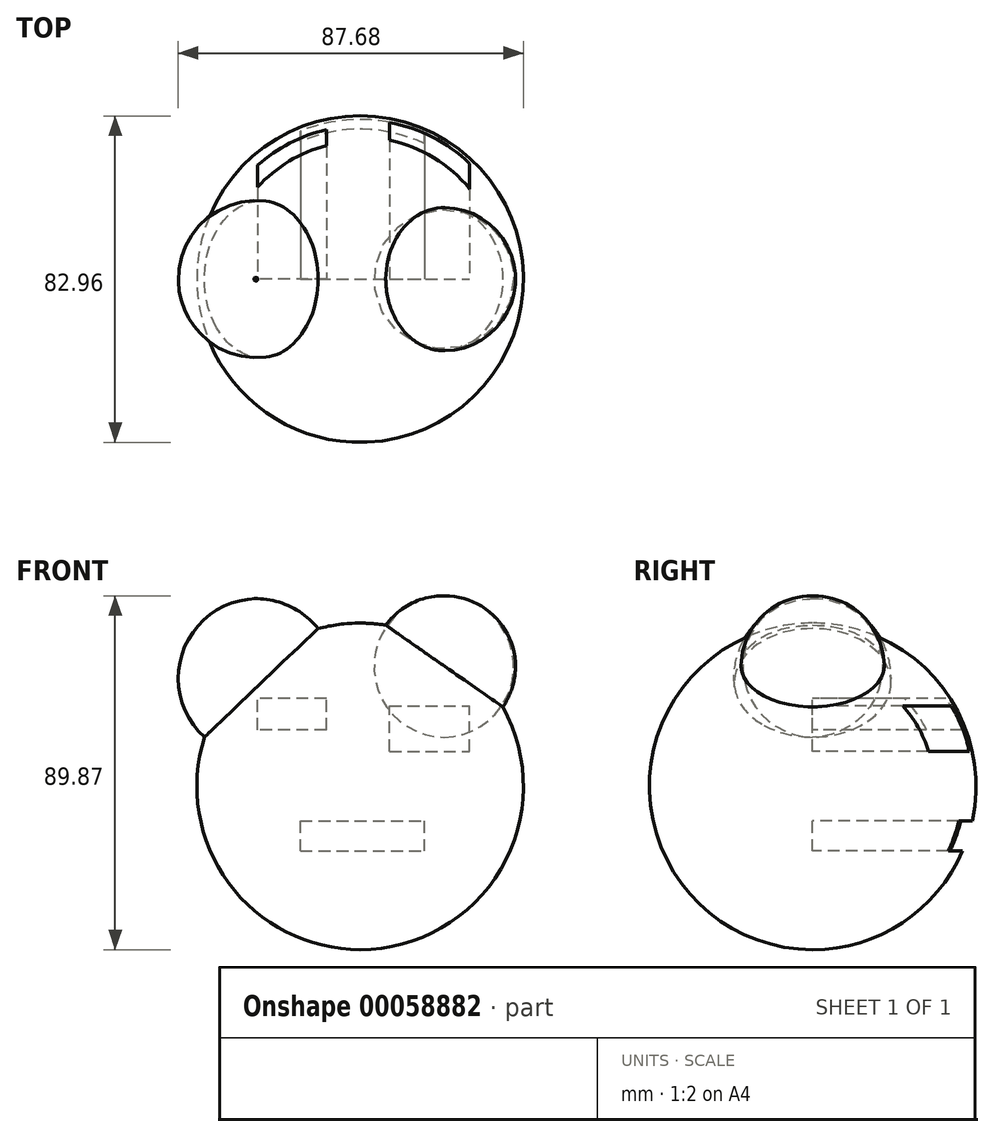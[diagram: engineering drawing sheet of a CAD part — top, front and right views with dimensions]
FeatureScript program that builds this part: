
annotation { "Feature Type Name" : "Feature", "Feature Type Description" : "" }
export const myFeature = defineFeature(function(context is Context, id is Id, definition is map)
    precondition{}
    {
        {
            var Q0;
            Q0=qCreatedBy(makeId("Front.planeOp"),FACE);
            var sketch = newSketch(context, id + "F0", { "sketchPlane" : qUnion([Q0])});
            skCircle(sketch, "E0", {"center": v(0, 0) * mm, "radius": 41.48 * mm});
            skLineSegment(sketch, "E1", {"start": v(0, -41.48) * mm, "end": v(0, 41.48) * mm});
            skSolve(sketch);
        }
        {
            var Q0;
            {var subQ0=sQuery(id+"F0.wireOp",EDGE,"E1");Q0=makeQuery(id+"F0.imprint","IMPRINT",FACE,{"disambiguationData":[TD([[makeQuery(id+"F0.imprint","IMPRINT",EDGE,{"derivedFrom":subQ0}),1.0]])]});}
            var Q1;
            Q1=sQuery(id+"F0.wireOp",EDGE,"E1");
            revolve(context, id + "F1", {"entities" : qUnion([Q0]), "axis" : qUnion([Q1]), "revolveType" : RevolveType.FULL});
        }
        {
            var Q0;
            Q0=qCreatedBy(makeId("Front.planeOp"),FACE);
            var sketch = newSketch(context, id + "F2", { "sketchPlane" : qUnion([Q0])});
            skCircle(sketch, "E2", {"center": v(-26.48, 27.5) * mm, "radius": 20.19 * mm});
            skLineSegment(sketch, "E3", {"start": v(-26, 7.32) * mm, "end": v(-26.48, 47.69) * mm});
            skSolve(sketch);
        }
        {
            var Q0;
            {var subQ0=sQuery(id+"F2.wireOp",EDGE,"E3");Q0=makeQuery(id+"F2.imprint","IMPRINT",FACE,{"disambiguationData":[TD([[makeQuery(id+"F2.imprint","IMPRINT",EDGE,{"derivedFrom":subQ0}),-1.0]])]});}
            var Q1;
            Q1=sQuery(id+"F2.wireOp",EDGE,"E3");
            revolve(context, id + "F3", {"operationType" : NewBodyOperationType.ADD, "entities" : qUnion([Q0]), "axis" : qUnion([Q1]), "revolveType" : RevolveType.FULL});
        }
        {
            var Q0;
            Q0=qCreatedBy(makeId("Front.planeOp"),FACE);
            var sketch = newSketch(context, id + "F4", { "sketchPlane" : qUnion([Q0])});
            skCircle(sketch, "E4", {"center": v(21.5, 30.44) * mm, "radius": 17.95 * mm});
            skLineSegment(sketch, "E5", {"start": v(21.27, 12.5) * mm, "end": v(21.27, 48.4) * mm});
            skSolve(sketch);
        }
        {
            var Q0;
            {var subQ0=sQuery(id+"F4.wireOp",EDGE,"E5");Q0=makeQuery(id+"F4.imprint","IMPRINT",FACE,{"disambiguationData":[TD([[makeQuery(id+"F4.imprint","IMPRINT",EDGE,{"derivedFrom":subQ0}),-1.0]])]});}
            var Q1;
            Q1=sQuery(id+"F4.wireOp",EDGE,"E5");
            revolve(context, id + "F5", {"operationType" : NewBodyOperationType.ADD, "entities" : qUnion([Q0]), "axis" : qUnion([Q1]), "revolveType" : RevolveType.FULL});
        }
        {
            var Q0;
            Q0=qCreatedBy(makeId("Front.planeOp"),FACE);
            var sketch = newSketch(context, id + "F6", { "sketchPlane" : qUnion([Q0])});
            skLineSegment(sketch, "E6.bottom", {"start": v(-8.6, 14.37) * mm, "end": v(-26.03, 14.37) * mm});
            skLineSegment(sketch, "E6.top", {"start": v(-8.6, 22.3) * mm, "end": v(-26.03, 22.3) * mm});
            skLineSegment(sketch, "E6.left", {"start": v(-8.6, 14.37) * mm, "end": v(-8.6, 22.3) * mm});
            skLineSegment(sketch, "E6.right", {"start": v(-26.03, 14.37) * mm, "end": v(-26.03, 22.3) * mm});
            skSolve(sketch);
        }
        {
            var Q0;
            Q0 = qSketchRegion(id + "F6", true);
            extrude(context, id + "F7", {"entities" : qUnion([Q0]), "operationType" : NewBodyOperationType.REMOVE, "endBound" : BoundingType.THROUGH_ALL, "oppositeDirection" : true, "depth" : 25.4 * mm});
        }
        {
            var Q0;
            Q0 = qSketchRegion(id + "F6", true);
            extrude(context, id + "F8", {"entities" : qUnion([Q0]), "operationType" : NewBodyOperationType.REMOVE, "endBound" : BoundingType.THROUGH_ALL, "oppositeDirection" : true, "depth" : 25.4 * mm});
        }
        {
            var Q0;
            Q0=qCreatedBy(makeId("Front.planeOp"),FACE);
            var sketch = newSketch(context, id + "F9", { "sketchPlane" : qUnion([Q0])});
            skLineSegment(sketch, "E7.bottom", {"start": v(7.47, 8.94) * mm, "end": v(27.84, 8.94) * mm});
            skLineSegment(sketch, "E7.top", {"start": v(7.47, 20.48) * mm, "end": v(27.84, 20.48) * mm});
            skLineSegment(sketch, "E7.left", {"start": v(7.47, 8.94) * mm, "end": v(7.47, 20.48) * mm});
            skLineSegment(sketch, "E7.right", {"start": v(27.84, 8.94) * mm, "end": v(27.84, 20.48) * mm});
            skSolve(sketch);
        }
        {
            var Q0;
            Q0 = qSketchRegion(id + "F9", true);
            extrude(context, id + "F10", {"entities" : qUnion([Q0]), "operationType" : NewBodyOperationType.REMOVE, "endBound" : BoundingType.THROUGH_ALL, "oppositeDirection" : true, "depth" : 25.4 * mm});
        }
        {
            var Q0;
            Q0=qCreatedBy(makeId("Front.planeOp"),FACE);
            var sketch = newSketch(context, id + "F11", { "sketchPlane" : qUnion([Q0])});
            skLineSegment(sketch, "E8.bottom", {"start": v(-15.16, -16.4) * mm, "end": v(16.3, -16.4) * mm});
            skLineSegment(sketch, "E8.top", {"start": v(-15.16, -8.71) * mm, "end": v(16.3, -8.71) * mm});
            skLineSegment(sketch, "E8.left", {"start": v(-15.16, -16.4) * mm, "end": v(-15.16, -8.71) * mm});
            skLineSegment(sketch, "E8.right", {"start": v(16.3, -16.4) * mm, "end": v(16.3, -8.71) * mm});
            skSolve(sketch);
        }
        {
            var Q0;
            Q0 = qSketchRegion(id + "F11", true);
            extrude(context, id + "F12", {"entities" : qUnion([Q0]), "operationType" : NewBodyOperationType.REMOVE, "endBound" : BoundingType.THROUGH_ALL, "oppositeDirection" : true, "depth" : 25.4 * mm});
        }
    });
